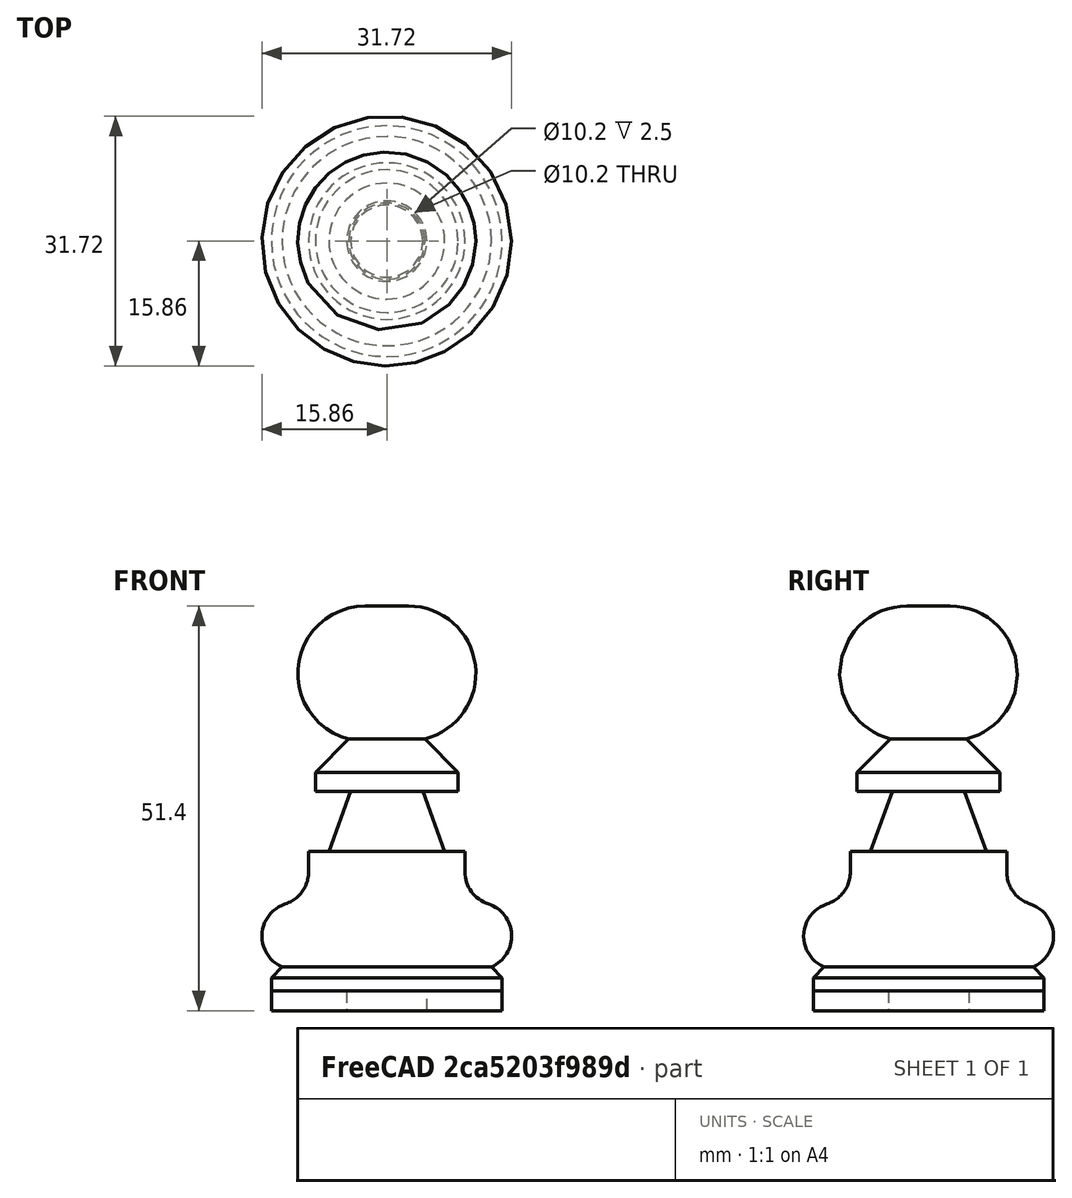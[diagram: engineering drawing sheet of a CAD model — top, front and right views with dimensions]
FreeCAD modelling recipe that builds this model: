
FCSTD DOCUMENT  (FreeCAD 0.19R23578 (Git))
Label: pawn
License: All rights reserved
LicenseURL: http://en.wikipedia.org/wiki/All_rights_reserved
objects: Sketcher::SketchObject×3, PartDesign::Body×2, App::Part×2, PartDesign::Revolution×1, PartDesign::Pocket×1, PartDesign::Pad×1, Mesh::Feature×1
note: 11 computed .brp shape members not serialized (recipe doc carries the construction recipe); baked Part::Feature solids carry a one-line shape summary decoded from their .brp

FEATURE [Sketcher::SketchObject] Sketch
  MapMode = 5
  Placement = pos=(0,0,0) rot=(1,0,0;1.5708rad)
  Support = -> [XZ_Plane001]
  expr: .Constraints.pr = 14.65mm
  expr: Constraints[26] = 11.79 / 8.550000000000001 * .Constraints.pr
  expr: Constraints[38] = 2.67 / 8.550000000000001 * .Constraints.pr
  expr: Constraints[29] = 2.45 / 8.550000000000001 * .Constraints.pr
  expr: Constraints[32] = 1.12 / 8.550000000000001 * .Constraints.pr
  expr: Constraints[22] = 5.29 / 8.550000000000001 * .Constraints.pr
  expr: Constraints[20] = 30 / 8.550000000000001 * .Constraints.pr
  expr: Constraints[25] = 16.26 / 8.550000000000001 * .Constraints.pr
  expr: Constraints[28] = 1.5 / 8.550000000000001 * .Constraints.pr
  expr: Constraints[37] = 1.6 / 8.550000000000001 * .Constraints.pr
  expr: Constraints[35] = 2.5 / 8.550000000000001 * .Constraints.pr
  expr: Constraints[36] = 5 / 8.550000000000001 * .Constraints.pr
  expr: Constraints[24] = 1.42 / 8.550000000000001 * .Constraints.pr
  sketch-geometry (14):
    g0: ArcOfCircle CenterX=2.74152 CenterY=42.8363 CenterZ=0 NormalX=0 NormalY=0 NormalZ=1 AngleXU=0 Radius=8.56725 StartAngle=4.95869 EndAngle=7.85398
    g1: LineSegment StartX=4.83039 StartY=34.5276 StartZ=0 EndX=9.06415 EndY=30.2938 EndZ=0
    g2: LineSegment StartX=9.06415 StartY=30.2938 StartZ=0 EndX=9.06415 EndY=27.8607 EndZ=0
    g3: LineSegment StartX=9.06415 StartY=27.8607 StartZ=0 EndX=4.57491 EndY=27.8607 EndZ=0
    g4: LineSegment StartX=4.57491 StartY=27.8607 StartZ=0 EndX=7.36261 EndY=20.2016 EndZ=0
    g5: LineSegment StartX=7.36261 StartY=20.2016 StartZ=0 EndX=9.93278 EndY=20.2016 EndZ=0
    g6: LineSegment StartX=9.93278 StartY=20.2016 StartZ=0 EndX=9.93278 EndY=17.6314 EndZ=0
    g7: ArcOfCircle CenterX=14.2164 CenterY=17.6314 CenterZ=0 NormalX=0 NormalY=0 NormalZ=1 AngleXU=0 Radius=4.28363 StartAngle=3.14159 EndAngle=4.39938
    g8: ArcOfCircle CenterX=11.5784 CenterY=9.48042 CenterZ=0 NormalX=0 NormalY=0 NormalZ=1 AngleXU=0 Radius=4.28363 StartAngle=5.12421 EndAngle=7.54097
    g9: LineSegment StartX=13.293 StartY=5.55494 StartZ=0 EndX=14.65 EndY=4.19795 EndZ=0
    g10: LineSegment StartX=14.65 StartY=4.19795 StartZ=0 EndX=14.65 EndY=0 EndZ=0
    g11: LineSegment StartX=14.65 StartY=0 StartZ=0 EndX=0 EndY=0 EndZ=0
    g12: LineSegment StartX=2.74152 StartY=51.4035 StartZ=0 EndX=0 EndY=51.4035 EndZ=0
    g13: LineSegment StartX=0 StartY=51.4035 StartZ=0 EndX=0 EndY=0 EndZ=0
  constraints (41):
    c: Coincident(g1,g0)
    c: Coincident(g2,g1)
    c: Coincident(g3,g2)
    c: Horizontal(g3)
    c: Coincident(g4,g3)
    c: Coincident(g5,g4)
    c: Horizontal(g5)
    c: Coincident(g6,g5)
    c: Vertical(g6)
    c: Coincident(g9,g8)
    c: PointOnObject(g10,g-1)
    c: Vertical(g10)
    c: Coincident(g11,g10)
    c: Coincident(g11,g-1)
    c: Horizontal(g12)
    c: PointOnObject(g12,g-2)
    c: Vertical(g2)
    c: Angle(g1,g3) = 0.785398
    c: Angle(g9,g11) = 0.785398
    c: Coincident(g9,g10)
    c: DistanceY(g-1,g12) = 51.4035
    c: DistanceX(g11,g11) = 14.65  'pr'
    c: DistanceX(g-2,g1) = 9.06415
    c: Tangent(g0,g12) = -1.5708
    c: DistanceY(g2,g2) = 2.4331
    c: DistanceY(g-1,g3) = 27.8607
    c: DistanceY(g-1,g4) = 20.2016
    c: Angle(g5,g4) = 1.91986
    c: DistanceX(g5,g5) = 2.57018
    c: DistanceY(g10,g10) = 4.19795
    c: Tangent(g6,g7) = -1.5708
    c: Tangent(g7,g8) = 1.5708
    c: Distance(g9) = 1.91906
    c: Equal(g7,g8)
    c: Equal(g5,g6)
    c: Radius(g7) = 4.28363
    c: Radius(g0) = 8.56725
    c: DistanceX(g12,g12) = 2.74152
    c: DistanceX(g-2,g3) = 4.57491
    c: Coincident(g13,g12)
    c: Coincident(g13,g11)
FEATURE [PartDesign::Revolution] Revolution
  Angle = 360
  Axis = (0,-2e-16,1)
  Base = (0,0,0)
  Placement = pos=(0,0,0) rot=(1,0,0;1.5708rad)
  Profile = -> Sketch
  ReferenceAxis = -> Sketch [V_Axis]
  Reversed = true
FEATURE [Sketcher::SketchObject] Sketch001
  MapMode = 5
  Placement = pos=(0,0,0) rot=(1,0,0;3.14159rad)
  Support = -> [Revolution]
  sketch-geometry (1):
    g0: Circle CenterX=0 CenterY=0 CenterZ=0 NormalX=0 NormalY=0 NormalZ=1 AngleXU=0 Radius=5.1
  constraints (2):
    c: Coincident(g0,g-1)
    c: Diameter(g0) = 10.2
FEATURE [PartDesign::Pocket] Pocket
  BaseFeature = -> Revolution
  Length = 2.5
  Length2 = 100
  Placement = pos=(0,0,0) rot=(1,0,0;1.5708rad)
  Profile = -> Sketch001
  Type = 0
FEATURE [PartDesign::Body] Body  label="PawnBody"
  Group = -> [Sketch,Revolution,Sketch001,Pocket]
  Origin = -> Origin001
  Tip = -> Pocket
FEATURE [App::Part] Part  label="PawnPart"
  Group = -> [Body]
  Origin = -> Origin
FEATURE [Sketcher::SketchObject] Sketch002
  MapMode = 5
  Support = -> [XY_Plane003]
  sketch-geometry (2):
    g0: Circle CenterX=0 CenterY=0 CenterZ=0 NormalX=0 NormalY=0 NormalZ=1 AngleXU=0 Radius=14.65
    g1: Circle CenterX=0 CenterY=0 CenterZ=0 NormalX=0 NormalY=0 NormalZ=1 AngleXU=0 Radius=5.1
  constraints (4):
    c: Coincident(g0,g-1)
    c: Radius(g0) = 14.65
    c: Coincident(g1,g0)
    c: Radius(g1) = 5.1
FEATURE [PartDesign::Pad] Pad
  Direction = (1,1,1)
  Length = 2.5
  Length2 = 100
  Profile = -> Sketch002
  Type = 0
FEATURE [PartDesign::Body] Body001  label="HolderBody"
  Group = -> [Sketch002,Pad]
  Origin = -> Origin003
  Tip = -> Pad
FEATURE [App::Part] Part001  label="HolderPart"
  Group = -> [Body001]
  Origin = -> Origin002
FEATURE [Mesh::Feature] Mesh  label="HolderBody (Meshed)"
